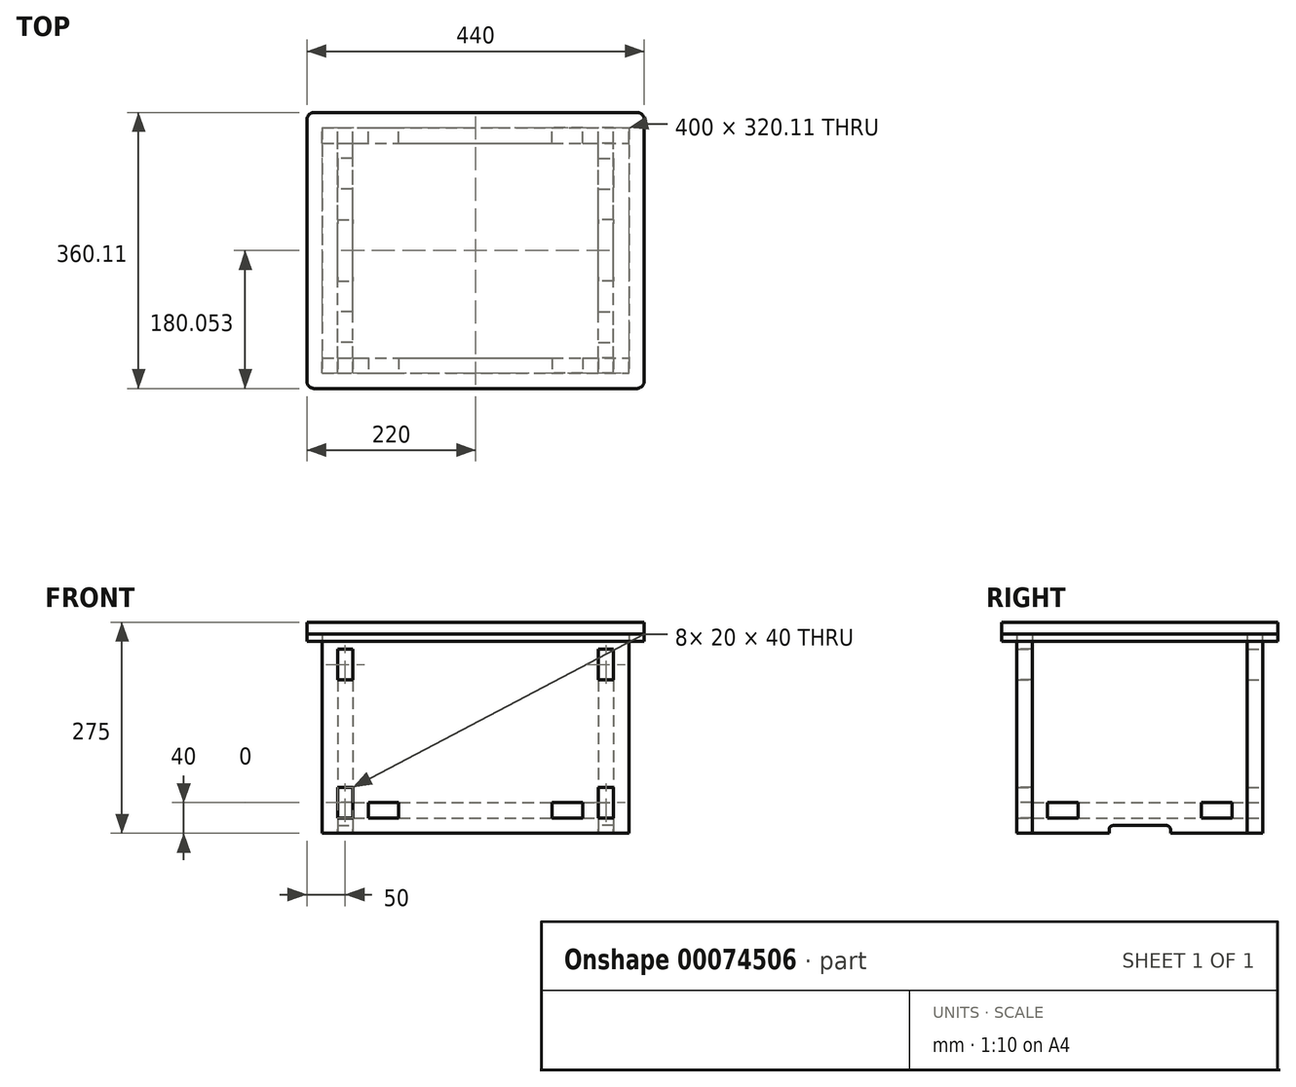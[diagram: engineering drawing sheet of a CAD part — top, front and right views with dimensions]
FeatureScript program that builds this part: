
annotation { "Feature Type Name" : "Feature", "Feature Type Description" : "" }
export const myFeature = defineFeature(function(context is Context, id is Id, definition is map)
    precondition{}
    {
        {
            var Q0;
            Q0=qCreatedBy(makeId("Front.planeOp"),FACE);
            var sketch = newSketch(context, id + "F0", { "sketchPlane" : qUnion([Q0])});
            skLineSegment(sketch, "E0.bottom", {"start": v(-200, 130) * mm, "end": v(200, 130) * mm});
            skLineSegment(sketch, "E0.top", {"start": v(-200, -130) * mm, "end": v(200, -130) * mm});
            skLineSegment(sketch, "E0.left", {"start": v(-200, 130) * mm, "end": v(-200, -130) * mm});
            skLineSegment(sketch, "E0.right", {"start": v(200, 130) * mm, "end": v(200, -130) * mm});
            skLineSegment(sketch, "E1", {"start": v(-200, 110) * mm, "end": v(200, 110) * mm, "construction": true});
            skLineSegment(sketch, "E2", {"start": v(-180, 130) * mm, "end": v(-180, -130) * mm, "construction": true});
            skLineSegment(sketch, "E3.bottom", {"start": v(-180, 110) * mm, "end": v(-160, 110) * mm});
            skLineSegment(sketch, "E3.top", {"start": v(-180, 70) * mm, "end": v(-160, 70) * mm});
            skLineSegment(sketch, "E3.left", {"start": v(-180, 110) * mm, "end": v(-180, 70) * mm});
            skLineSegment(sketch, "E3.right", {"start": v(-160, 110) * mm, "end": v(-160, 70) * mm});
            skLineSegment(sketch, "E4.MirrorCS", {"start": v(-180, -70) * mm, "end": v(-160, -70) * mm});
            skLineSegment(sketch, "E5.MirrorCS", {"start": v(-180, -110) * mm, "end": v(-160, -110) * mm});
            skLineSegment(sketch, "E6.MirrorCS", {"start": v(-160, -110) * mm, "end": v(-160, -70) * mm});
            skLineSegment(sketch, "E7.MirrorCS", {"start": v(-180, -110) * mm, "end": v(-180, -70) * mm});
            skLineSegment(sketch, "E8.MirrorCS", {"start": v(180, -110) * mm, "end": v(160, -110) * mm});
            skLineSegment(sketch, "E9.MirrorCS", {"start": v(180, -70) * mm, "end": v(160, -70) * mm});
            skLineSegment(sketch, "E10.MirrorCS", {"start": v(180, -110) * mm, "end": v(180, -70) * mm});
            skLineSegment(sketch, "E11.MirrorCS", {"start": v(160, -110) * mm, "end": v(160, -70) * mm});
            skLineSegment(sketch, "E12.MirrorCS", {"start": v(180, 110) * mm, "end": v(180, 70) * mm});
            skLineSegment(sketch, "E13.MirrorCS", {"start": v(180, 70) * mm, "end": v(160, 70) * mm});
            skLineSegment(sketch, "E14.MirrorCS", {"start": v(160, 110) * mm, "end": v(160, 70) * mm});
            skLineSegment(sketch, "E15.MirrorCS", {"start": v(180, 110) * mm, "end": v(160, 110) * mm});
            skSolve(sketch);
        }
        {
            var Q0;
            Q0 = qSketchRegion(id + "F0", true);
            extrude(context, id + "F1", {"entities" : qUnion([Q0]), "depth" : 20 * mm});
        }
        {
            var Q0;
            Q0=qCreatedBy(makeId("Right.planeOp"),FACE);
            var sketch = newSketch(context, id + "F2", { "sketchPlane" : qUnion([Q0])});
            skLineSegment(sketch, "E16", {"start": v(0, 130) * mm, "end": v(71.82, 130) * mm, "construction": true});
            skLineSegment(sketch, "E17", {"start": v(0, -130) * mm, "end": v(65.21, -130) * mm, "construction": true});
            skLineSegment(sketch, "E18.bottom", {"start": v(71.82, 130) * mm, "end": v(351.82, 130) * mm});
            skLineSegment(sketch, "E18.top", {"start": v(71.82, -130) * mm, "end": v(351.82, -130) * mm});
            skLineSegment(sketch, "E18.left", {"start": v(71.82, 130) * mm, "end": v(71.82, -130) * mm});
            skLineSegment(sketch, "E18.right", {"start": v(351.82, 130) * mm, "end": v(351.82, -130) * mm});
            skLineSegment(sketch, "E19", {"start": v(71.82, 110) * mm, "end": v(351.82, 110) * mm, "construction": true});
            skLineSegment(sketch, "E20.bottom", {"start": v(71.82, 110) * mm, "end": v(51.82, 110) * mm});
            skLineSegment(sketch, "E20.top", {"start": v(71.82, 70) * mm, "end": v(51.82, 70) * mm});
            skLineSegment(sketch, "E20.left", {"start": v(71.82, 110) * mm, "end": v(71.82, 70) * mm});
            skLineSegment(sketch, "E20.right", {"start": v(51.82, 110) * mm, "end": v(51.82, 70) * mm});
            skLineSegment(sketch, "E21.MirrorCS", {"start": v(71.82, -110) * mm, "end": v(51.82, -110) * mm});
            skLineSegment(sketch, "E22.MirrorCS", {"start": v(51.82, -110) * mm, "end": v(51.82, -70) * mm});
            skLineSegment(sketch, "E23.MirrorCS", {"start": v(71.82, -70) * mm, "end": v(51.82, -70) * mm});
            skLineSegment(sketch, "E24.MirrorCS", {"start": v(71.82, -110) * mm, "end": v(71.82, -70) * mm});
            skLineSegment(sketch, "E25", {"start": v(211.82, 130) * mm, "end": v(211.82, -130) * mm, "construction": true});
            skLineSegment(sketch, "E26.MirrorCS", {"start": v(351.82, 110) * mm, "end": v(371.82, 110) * mm});
            skLineSegment(sketch, "E27.MirrorCS", {"start": v(351.82, 70) * mm, "end": v(371.82, 70) * mm});
            skLineSegment(sketch, "E28.MirrorCS", {"start": v(351.82, 110) * mm, "end": v(351.82, 70) * mm});
            skLineSegment(sketch, "E29.MirrorCS", {"start": v(371.82, 110) * mm, "end": v(371.82, 70) * mm});
            skLineSegment(sketch, "E30.MirrorCS", {"start": v(351.82, -110) * mm, "end": v(351.82, -70) * mm});
            skLineSegment(sketch, "E31.MirrorCS", {"start": v(351.82, -70) * mm, "end": v(371.82, -70) * mm});
            skLineSegment(sketch, "E32.MirrorCS", {"start": v(351.82, -110) * mm, "end": v(371.82, -110) * mm});
            skLineSegment(sketch, "E33.MirrorCS", {"start": v(371.82, -110) * mm, "end": v(371.82, -70) * mm});
            skLineSegment(sketch, "E34.bottom", {"start": v(171.82, -130) * mm, "end": v(251.82, -130) * mm});
            skLineSegment(sketch, "E34.top", {"start": v(176.82, -120) * mm, "end": v(246.82, -120) * mm});
            skLineSegment(sketch, "E34.left", {"start": v(171.82, -130) * mm, "end": v(171.82, -125) * mm});
            skLineSegment(sketch, "E34.right", {"start": v(251.82, -130) * mm, "end": v(251.82, -125) * mm});
            skPoint(sketch, "E35.visualSharp", {"position": v(171.82, -120) * mm});
            skArc(sketch, "E35.filletArc", {"start": v(176.82, -120) * mm, "mid": v(173.28, -121.46) * mm, "end": v(171.82, -125) * mm});
            skPoint(sketch, "E36.visualSharp", {"position": v(251.82, -120) * mm});
            skArc(sketch, "E36.filletArc", {"start": v(251.82, -125) * mm, "mid": v(250.35, -121.46) * mm, "end": v(246.82, -120) * mm});
            skSolve(sketch);
        }
        {
            var Q0;
            Q0=makeQuery(id+"F2.imprint","IMPRINT",FACE,{"disambiguationData":[TD([[makeQuery(id+"F2.imprint","IMPRINT",EDGE,{"derivedFrom":sQuery(id+"F2.wireOp",EDGE,"E20.bottom")}),1.0]])]});
            var Q1;
            Q1=makeQuery(id+"F2.imprint","IMPRINT",FACE,{"disambiguationData":[TD([[makeQuery(id+"F2.imprint","IMPRINT",EDGE,{"derivedFrom":sQuery(id+"F2.wireOp",EDGE,"E21.MirrorCS")}),-1.0]])]});
            var Q2;
            Q2=makeQuery(id+"F2.imprint","IMPRINT",FACE,{"disambiguationData":[TD([[makeQuery(id+"F2.imprint","IMPRINT",EDGE,{"derivedFrom":sQuery(id+"F2.wireOp",EDGE,"E26.MirrorCS")}),-1.0]])]});
            var Q3;
            Q3=makeQuery(id+"F2.imprint","IMPRINT",FACE,{"disambiguationData":[TD([[makeQuery(id+"F2.imprint","IMPRINT",EDGE,{"derivedFrom":sQuery(id+"F2.wireOp",EDGE,"E30.MirrorCS")}),-1.0]])]});
            var Q4;
            {var subQ5=sQuery(id+"F2.wireOp",EDGE,"E18.bottom");Q4=makeQuery(id+"F2.imprint","IMPRINT",FACE,{"disambiguationData":[TD([[makeQuery(id+"F2.imprint","IMPRINT",EDGE,{"derivedFrom":subQ5}),-1.0]])]});}
            extrude(context, id + "F3", {"entities" : qUnion([Q0, Q1, Q2, Q3, Q4]), "endBound" : BoundingType.SYMMETRIC, "depth" : 20 * mm});
        }
        {
            var Q0;
            Q0=makeQuery(id+"F3.opExtrude","SWEPT_BODY",BODY,{"disambiguationData":[OSD([sQuery(id+"F2.wireOp",EDGE,"E18.bottom"),sQuery(id+"F2.wireOp",EDGE,"E18.top"),sQuery(id+"F2.wireOp",EDGE,"E18.left"),sQuery(id+"F2.wireOp",EDGE,"E18.right"),sQuery(id+"F2.wireOp",EDGE,"E20.bottom"),sQuery(id+"F2.wireOp",EDGE,"E20.top"),sQuery(id+"F2.wireOp",EDGE,"E20.right"),sQuery(id+"F2.wireOp",EDGE,"E21.MirrorCS"),sQuery(id+"F2.wireOp",EDGE,"E22.MirrorCS"),sQuery(id+"F2.wireOp",EDGE,"E23.MirrorCS"),sQuery(id+"F2.wireOp",EDGE,"E26.MirrorCS"),sQuery(id+"F2.wireOp",EDGE,"E27.MirrorCS"),sQuery(id+"F2.wireOp",EDGE,"E29.MirrorCS"),sQuery(id+"F2.wireOp",EDGE,"E31.MirrorCS"),sQuery(id+"F2.wireOp",EDGE,"E32.MirrorCS"),sQuery(id+"F2.wireOp",EDGE,"E33.MirrorCS")])]});
            var Q1;
            Q1=qCreatedBy(makeId("Right.planeOp"),FACE);
            mirror(context, id + "F4", {"operationType" : NewBodyOperationType.ADD, "entities" : qUnion([Q0]), "mirrorPlane" : qUnion([Q1])});
        }
        {
            var Q0;
            Q0=makeQuery(id+"F1.opExtrude","SWEPT_BODY",BODY,{"disambiguationData":[OSD([sQuery(id+"F0.wireOp",EDGE,"E0.bottom"),sQuery(id+"F0.wireOp",EDGE,"E0.top"),sQuery(id+"F0.wireOp",EDGE,"E0.left"),sQuery(id+"F0.wireOp",EDGE,"E0.right"),sQuery(id+"F0.wireOp",EDGE,"E3.bottom"),sQuery(id+"F0.wireOp",EDGE,"E3.top"),sQuery(id+"F0.wireOp",EDGE,"E3.left"),sQuery(id+"F0.wireOp",EDGE,"E3.right"),sQuery(id+"F0.wireOp",EDGE,"E4.MirrorCS"),sQuery(id+"F0.wireOp",EDGE,"E5.MirrorCS"),sQuery(id+"F0.wireOp",EDGE,"E6.MirrorCS"),sQuery(id+"F0.wireOp",EDGE,"E7.MirrorCS"),sQuery(id+"F0.wireOp",EDGE,"E8.MirrorCS"),sQuery(id+"F0.wireOp",EDGE,"E9.MirrorCS"),sQuery(id+"F0.wireOp",EDGE,"E10.MirrorCS"),sQuery(id+"F0.wireOp",EDGE,"E11.MirrorCS"),sQuery(id+"F0.wireOp",EDGE,"E12.MirrorCS"),sQuery(id+"F0.wireOp",EDGE,"E13.MirrorCS"),sQuery(id+"F0.wireOp",EDGE,"E14.MirrorCS"),sQuery(id+"F0.wireOp",EDGE,"E15.MirrorCS")])]});
            transform(context, id + "F5", {"entities" : qUnion([Q0]), "transformType" : TransformType.TRANSLATION_3D, "dx" : 0 * mm, "dy" : 371.83 * mm, "dz" : 0 * mm, "makeCopy" : true});
        }
        {
            var Q0;
            Q0=makeQuery(id+"F3.opExtrude","SWEPT_BODY",BODY,{"disambiguationData":[OSD([sQuery(id+"F2.wireOp",EDGE,"E18.bottom"),sQuery(id+"F2.wireOp",EDGE,"E18.top"),sQuery(id+"F2.wireOp",EDGE,"E18.left"),sQuery(id+"F2.wireOp",EDGE,"E18.right"),sQuery(id+"F2.wireOp",EDGE,"E20.bottom"),sQuery(id+"F2.wireOp",EDGE,"E20.top"),sQuery(id+"F2.wireOp",EDGE,"E20.right"),sQuery(id+"F2.wireOp",EDGE,"E21.MirrorCS"),sQuery(id+"F2.wireOp",EDGE,"E22.MirrorCS"),sQuery(id+"F2.wireOp",EDGE,"E23.MirrorCS"),sQuery(id+"F2.wireOp",EDGE,"E26.MirrorCS"),sQuery(id+"F2.wireOp",EDGE,"E27.MirrorCS"),sQuery(id+"F2.wireOp",EDGE,"E29.MirrorCS"),sQuery(id+"F2.wireOp",EDGE,"E31.MirrorCS"),sQuery(id+"F2.wireOp",EDGE,"E32.MirrorCS"),sQuery(id+"F2.wireOp",EDGE,"E33.MirrorCS")])]});
            var Q1;
            Q1=makeQuery(id+"F4.opPattern","COPY",BODY,{"derivedFrom":makeQuery(id+"F3.opExtrude","SWEPT_BODY",BODY,{"disambiguationData":[OSD([sQuery(id+"F2.wireOp",EDGE,"E18.bottom"),sQuery(id+"F2.wireOp",EDGE,"E18.top"),sQuery(id+"F2.wireOp",EDGE,"E18.left"),sQuery(id+"F2.wireOp",EDGE,"E18.right"),sQuery(id+"F2.wireOp",EDGE,"E20.bottom"),sQuery(id+"F2.wireOp",EDGE,"E20.top"),sQuery(id+"F2.wireOp",EDGE,"E20.right"),sQuery(id+"F2.wireOp",EDGE,"E21.MirrorCS"),sQuery(id+"F2.wireOp",EDGE,"E22.MirrorCS"),sQuery(id+"F2.wireOp",EDGE,"E23.MirrorCS"),sQuery(id+"F2.wireOp",EDGE,"E26.MirrorCS"),sQuery(id+"F2.wireOp",EDGE,"E27.MirrorCS"),sQuery(id+"F2.wireOp",EDGE,"E29.MirrorCS"),sQuery(id+"F2.wireOp",EDGE,"E31.MirrorCS"),sQuery(id+"F2.wireOp",EDGE,"E32.MirrorCS"),sQuery(id+"F2.wireOp",EDGE,"E33.MirrorCS")])]}),"instanceName":"1"});
            var Q2;
            Q2=makeQuery(id+"F5.opPattern","COPY",BODY,{"derivedFrom":makeQuery(id+"F1.opExtrude","SWEPT_BODY",BODY,{"disambiguationData":[OSD([sQuery(id+"F0.wireOp",EDGE,"E0.bottom"),sQuery(id+"F0.wireOp",EDGE,"E0.top"),sQuery(id+"F0.wireOp",EDGE,"E0.left"),sQuery(id+"F0.wireOp",EDGE,"E0.right"),sQuery(id+"F0.wireOp",EDGE,"E3.bottom"),sQuery(id+"F0.wireOp",EDGE,"E3.top"),sQuery(id+"F0.wireOp",EDGE,"E3.left"),sQuery(id+"F0.wireOp",EDGE,"E3.right"),sQuery(id+"F0.wireOp",EDGE,"E4.MirrorCS"),sQuery(id+"F0.wireOp",EDGE,"E5.MirrorCS"),sQuery(id+"F0.wireOp",EDGE,"E6.MirrorCS"),sQuery(id+"F0.wireOp",EDGE,"E7.MirrorCS"),sQuery(id+"F0.wireOp",EDGE,"E8.MirrorCS"),sQuery(id+"F0.wireOp",EDGE,"E9.MirrorCS"),sQuery(id+"F0.wireOp",EDGE,"E10.MirrorCS"),sQuery(id+"F0.wireOp",EDGE,"E11.MirrorCS"),sQuery(id+"F0.wireOp",EDGE,"E12.MirrorCS"),sQuery(id+"F0.wireOp",EDGE,"E13.MirrorCS"),sQuery(id+"F0.wireOp",EDGE,"E14.MirrorCS"),sQuery(id+"F0.wireOp",EDGE,"E15.MirrorCS")])]}),"instanceName":"1"});
            transform(context, id + "F6", {"entities" : qUnion([Q0, Q1, Q2]), "transformType" : TransformType.TRANSLATION_3D, "dx" : 0 * mm, "dy" : -71.72 * mm, "dz" : 0 * mm, "makeCopy" : false});
        }
        {
            var Q0;
            Q0=makeQuery(id+"F3.opExtrude","SWEPT_BODY",BODY,{"disambiguationData":[OSD([sQuery(id+"F2.wireOp",EDGE,"E18.bottom"),sQuery(id+"F2.wireOp",EDGE,"E18.top"),sQuery(id+"F2.wireOp",EDGE,"E18.left"),sQuery(id+"F2.wireOp",EDGE,"E18.right"),sQuery(id+"F2.wireOp",EDGE,"E20.bottom"),sQuery(id+"F2.wireOp",EDGE,"E20.top"),sQuery(id+"F2.wireOp",EDGE,"E20.right"),sQuery(id+"F2.wireOp",EDGE,"E21.MirrorCS"),sQuery(id+"F2.wireOp",EDGE,"E22.MirrorCS"),sQuery(id+"F2.wireOp",EDGE,"E23.MirrorCS"),sQuery(id+"F2.wireOp",EDGE,"E26.MirrorCS"),sQuery(id+"F2.wireOp",EDGE,"E27.MirrorCS"),sQuery(id+"F2.wireOp",EDGE,"E29.MirrorCS"),sQuery(id+"F2.wireOp",EDGE,"E31.MirrorCS"),sQuery(id+"F2.wireOp",EDGE,"E32.MirrorCS"),sQuery(id+"F2.wireOp",EDGE,"E33.MirrorCS")])]});
            transform(context, id + "F7", {"entities" : qUnion([Q0]), "transformType" : TransformType.TRANSLATION_3D, "dx" : 170 * mm, "dy" : 0 * mm, "dz" : 0 * mm, "makeCopy" : false});
        }
        {
            var Q0;
            Q0=makeQuery(id+"F4.opPattern","COPY",BODY,{"derivedFrom":makeQuery(id+"F3.opExtrude","SWEPT_BODY",BODY,{"disambiguationData":[OSD([sQuery(id+"F2.wireOp",EDGE,"E18.bottom"),sQuery(id+"F2.wireOp",EDGE,"E18.top"),sQuery(id+"F2.wireOp",EDGE,"E18.left"),sQuery(id+"F2.wireOp",EDGE,"E18.right"),sQuery(id+"F2.wireOp",EDGE,"E20.bottom"),sQuery(id+"F2.wireOp",EDGE,"E20.top"),sQuery(id+"F2.wireOp",EDGE,"E20.right"),sQuery(id+"F2.wireOp",EDGE,"E21.MirrorCS"),sQuery(id+"F2.wireOp",EDGE,"E22.MirrorCS"),sQuery(id+"F2.wireOp",EDGE,"E23.MirrorCS"),sQuery(id+"F2.wireOp",EDGE,"E26.MirrorCS"),sQuery(id+"F2.wireOp",EDGE,"E27.MirrorCS"),sQuery(id+"F2.wireOp",EDGE,"E29.MirrorCS"),sQuery(id+"F2.wireOp",EDGE,"E31.MirrorCS"),sQuery(id+"F2.wireOp",EDGE,"E32.MirrorCS"),sQuery(id+"F2.wireOp",EDGE,"E33.MirrorCS")])]}),"instanceName":"1"});
            transform(context, id + "F8", {"entities" : qUnion([Q0]), "transformType" : TransformType.TRANSLATION_3D, "dx" : -170 * mm, "dy" : 0 * mm, "dz" : 0 * mm, "makeCopy" : false});
        }
        {
            var Q0;
            Q0=qCreatedBy(makeId("Top.planeOp"),FACE);
            cPlane(context, id + "F9", {"entities" : qUnion([Q0]), "cplaneType" : CPlaneType.OFFSET, "offset" : 130 * mm, "width" : 150 * mm, "height" : 150 * mm});
        }
        {
            var Q0;
            Q0=qCreatedBy(id+"F9.planeOp",FACE);
            var sketch = newSketch(context, id + "F10", { "sketchPlane" : qUnion([Q0])});
            skLineSegment(sketch, "E37.bottom", {"start": v(-200, 300.1) * mm, "end": v(200, 300.1) * mm});
            skLineSegment(sketch, "E37.top", {"start": v(-200, -20) * mm, "end": v(200, -20) * mm});
            skLineSegment(sketch, "E37.left", {"start": v(-200, 300.1) * mm, "end": v(-200, -20) * mm});
            skLineSegment(sketch, "E37.right", {"start": v(200, 300.1) * mm, "end": v(200, -20) * mm});
            skLineSegment(sketch, "E38.0", {"start": v(-220, 310.1) * mm, "end": v(-220, -30) * mm});
            skLineSegment(sketch, "E38.1", {"start": v(-210, 320.1) * mm, "end": v(210, 320.1) * mm});
            skLineSegment(sketch, "E38.2", {"start": v(220, 310.1) * mm, "end": v(220, -30) * mm});
            skLineSegment(sketch, "E38.3", {"start": v(-210, -40) * mm, "end": v(210, -40) * mm});
            skPoint(sketch, "E39.visualSharp", {"position": v(-220, 320.1) * mm});
            skArc(sketch, "E39.filletArc", {"start": v(-210, 320.1) * mm, "mid": v(-217.07, 317.18) * mm, "end": v(-220, 310.1) * mm});
            skPoint(sketch, "E40.visualSharp", {"position": v(-220, -40) * mm});
            skArc(sketch, "E40.filletArc", {"start": v(-220, -30) * mm, "mid": v(-217.07, -37.07) * mm, "end": v(-210, -40) * mm});
            skPoint(sketch, "E41.visualSharp", {"position": v(220, -40) * mm});
            skArc(sketch, "E41.filletArc", {"start": v(210, -40) * mm, "mid": v(217.07, -37.07) * mm, "end": v(220, -30) * mm});
            skPoint(sketch, "E42.visualSharp", {"position": v(220, 320.1) * mm});
            skArc(sketch, "E42.filletArc", {"start": v(220, 310.1) * mm, "mid": v(217.07, 317.18) * mm, "end": v(210, 320.1) * mm});
            skSolve(sketch);
        }
        {
            var Q0;
            Q0 = qSketchRegion(id + "F10", true);
            extrude(context, id + "F11", {"entities" : qUnion([Q0]), "oppositeDirection" : true, "depth" : 10 * mm});
        }
        {
            var Q0;
            Q0 = qSketchRegion(id + "F10", true);
            var Q1;
            Q1=makeQuery(id+"F10.imprint","IMPRINT",FACE,{"disambiguationData":[TD([[makeQuery(id+"F10.imprint","IMPRINT",EDGE,{"derivedFrom":sQuery(id+"F10.wireOp",EDGE,"E37.bottom")}),-1.0]])]});
            extrude(context, id + "F12", {"entities" : qUnion([Q0, Q1]), "depth" : 15 * mm});
        }
        {
            var Q0;
            Q0=qCreatedBy(makeId("Top.planeOp"),FACE);
            cPlane(context, id + "F13", {"entities" : qUnion([Q0]), "cplaneType" : CPlaneType.OFFSET, "offset" : 130 * mm, "oppositeDirection" : true, "width" : 150 * mm, "height" : 150 * mm});
        }
        {
            var Q0;
            Q0=qCreatedBy(id+"F13.planeOp",FACE);
            var sketch = newSketch(context, id + "F14", { "sketchPlane" : qUnion([Q0])});
            skLineSegment(sketch, "E43.bottom", {"start": v(-160, 0) * mm, "end": v(160, 0) * mm});
            skLineSegment(sketch, "E43.top", {"start": v(-160, 280.1) * mm, "end": v(160, 280.1) * mm});
            skLineSegment(sketch, "E43.left", {"start": v(-160, 0) * mm, "end": v(-160, 280.1) * mm});
            skLineSegment(sketch, "E43.right", {"start": v(160, 0) * mm, "end": v(160, 280.1) * mm});
            skLineSegment(sketch, "E44", {"start": v(-140, 280.1) * mm, "end": v(-140, 0) * mm, "construction": true});
            skLineSegment(sketch, "E45", {"start": v(-160, 260.1) * mm, "end": v(160, 260.1) * mm, "construction": true});
            skLineSegment(sketch, "E46.bottom", {"start": v(-160, 260.1) * mm, "end": v(-180, 260.1) * mm});
            skLineSegment(sketch, "E46.top", {"start": v(-160, 220.1) * mm, "end": v(-180, 220.1) * mm});
            skLineSegment(sketch, "E46.left", {"start": v(-160, 260.1) * mm, "end": v(-160, 220.1) * mm});
            skLineSegment(sketch, "E46.right", {"start": v(-180, 260.1) * mm, "end": v(-180, 220.1) * mm});
            skLineSegment(sketch, "E47", {"start": v(160, 140.05) * mm, "end": v(-160, 140.05) * mm, "construction": true});
            skLineSegment(sketch, "E48.MirrorCS", {"start": v(-180, 20) * mm, "end": v(-180, 60) * mm});
            skLineSegment(sketch, "E49.MirrorCS", {"start": v(-160, 20) * mm, "end": v(-160, 60) * mm});
            skLineSegment(sketch, "E50.MirrorCS", {"start": v(-160, 20) * mm, "end": v(-180, 20) * mm});
            skLineSegment(sketch, "E51.MirrorCS", {"start": v(-160, 60) * mm, "end": v(-180, 60) * mm});
            skLineSegment(sketch, "E52.bottom", {"start": v(-140, 280.1) * mm, "end": v(-100, 280.1) * mm});
            skLineSegment(sketch, "E52.top", {"start": v(-140, 300.1) * mm, "end": v(-100, 300.1) * mm});
            skLineSegment(sketch, "E52.left", {"start": v(-140, 280.1) * mm, "end": v(-140, 300.1) * mm});
            skLineSegment(sketch, "E52.right", {"start": v(-100, 280.1) * mm, "end": v(-100, 300.1) * mm});
            skLineSegment(sketch, "E53.MirrorCS", {"start": v(100, 280.1) * mm, "end": v(100, 300.1) * mm});
            skLineSegment(sketch, "E54.MirrorCS", {"start": v(140, 300.1) * mm, "end": v(100, 300.1) * mm});
            skLineSegment(sketch, "E55.MirrorCS", {"start": v(140, 280.1) * mm, "end": v(100, 280.1) * mm});
            skLineSegment(sketch, "E56.MirrorCS", {"start": v(140, 280.1) * mm, "end": v(140, 300.1) * mm});
            skLineSegment(sketch, "E57.MirrorCS", {"start": v(180, 260.1) * mm, "end": v(180, 220.1) * mm});
            skLineSegment(sketch, "E58.MirrorCS", {"start": v(160, 260.1) * mm, "end": v(160, 220.1) * mm});
            skLineSegment(sketch, "E59.MirrorCS", {"start": v(160, 220.1) * mm, "end": v(180, 220.1) * mm});
            skLineSegment(sketch, "E60.MirrorCS", {"start": v(160, 260.1) * mm, "end": v(180, 260.1) * mm});
            skLineSegment(sketch, "E61.MirrorCS", {"start": v(180, 20) * mm, "end": v(180, 60) * mm});
            skLineSegment(sketch, "E62.MirrorCS", {"start": v(160, 20) * mm, "end": v(160, 60) * mm});
            skLineSegment(sketch, "E63.MirrorCS", {"start": v(160, 60) * mm, "end": v(180, 60) * mm});
            skLineSegment(sketch, "E64.MirrorCS", {"start": v(160, 20) * mm, "end": v(180, 20) * mm});
            skLineSegment(sketch, "E65.MirrorCS", {"start": v(100, 0) * mm, "end": v(100, -20) * mm});
            skLineSegment(sketch, "E66.MirrorCS", {"start": v(140, 0) * mm, "end": v(140, -20) * mm});
            skLineSegment(sketch, "E67.MirrorCS", {"start": v(-100, 0) * mm, "end": v(-100, -20) * mm});
            skLineSegment(sketch, "E68.MirrorCS", {"start": v(-140, 0) * mm, "end": v(-140, -20) * mm});
            skLineSegment(sketch, "E69.MirrorCS", {"start": v(140, -20) * mm, "end": v(100, -20) * mm});
            skLineSegment(sketch, "E70.MirrorCS", {"start": v(140, 0) * mm, "end": v(100, 0) * mm});
            skLineSegment(sketch, "E71.MirrorCS", {"start": v(-140, 0) * mm, "end": v(-100, 0) * mm});
            skLineSegment(sketch, "E72.MirrorCS", {"start": v(-140, -20) * mm, "end": v(-100, -20) * mm});
            skSolve(sketch);
        }
        {
            var Q0;
            Q0 = qSketchRegion(id + "F14", true);
            extrude(context, id + "F15", {"entities" : qUnion([Q0]), "depth" : 20 * mm});
        }
        {
            var Q0;
            Q0=makeQuery(id+"F15.opExtrude","SWEPT_BODY",BODY,{"disambiguationData":[OSD([sQuery(id+"F14.wireOp",EDGE,"E43.bottom"),sQuery(id+"F14.wireOp",EDGE,"E43.top"),sQuery(id+"F14.wireOp",EDGE,"E43.left"),sQuery(id+"F14.wireOp",EDGE,"E43.right"),sQuery(id+"F14.wireOp",EDGE,"E46.bottom"),sQuery(id+"F14.wireOp",EDGE,"E46.top"),sQuery(id+"F14.wireOp",EDGE,"E46.right"),sQuery(id+"F14.wireOp",EDGE,"E48.MirrorCS"),sQuery(id+"F14.wireOp",EDGE,"E50.MirrorCS"),sQuery(id+"F14.wireOp",EDGE,"E51.MirrorCS"),sQuery(id+"F14.wireOp",EDGE,"E52.top"),sQuery(id+"F14.wireOp",EDGE,"E52.left"),sQuery(id+"F14.wireOp",EDGE,"E52.right"),sQuery(id+"F14.wireOp",EDGE,"E53.MirrorCS"),sQuery(id+"F14.wireOp",EDGE,"E54.MirrorCS"),sQuery(id+"F14.wireOp",EDGE,"E56.MirrorCS"),sQuery(id+"F14.wireOp",EDGE,"E57.MirrorCS"),sQuery(id+"F14.wireOp",EDGE,"E59.MirrorCS"),sQuery(id+"F14.wireOp",EDGE,"E60.MirrorCS"),sQuery(id+"F14.wireOp",EDGE,"E61.MirrorCS"),sQuery(id+"F14.wireOp",EDGE,"E63.MirrorCS"),sQuery(id+"F14.wireOp",EDGE,"E64.MirrorCS"),sQuery(id+"F14.wireOp",EDGE,"E65.MirrorCS"),sQuery(id+"F14.wireOp",EDGE,"E66.MirrorCS"),sQuery(id+"F14.wireOp",EDGE,"E67.MirrorCS"),sQuery(id+"F14.wireOp",EDGE,"E68.MirrorCS"),sQuery(id+"F14.wireOp",EDGE,"E69.MirrorCS"),sQuery(id+"F14.wireOp",EDGE,"E72.MirrorCS")])]});
            transform(context, id + "F16", {"entities" : qUnion([Q0]), "transformType" : TransformType.TRANSLATION_3D, "dx" : 0 * mm, "dy" : 0 * mm, "dz" : 20 * mm, "makeCopy" : false});
        }
    });
